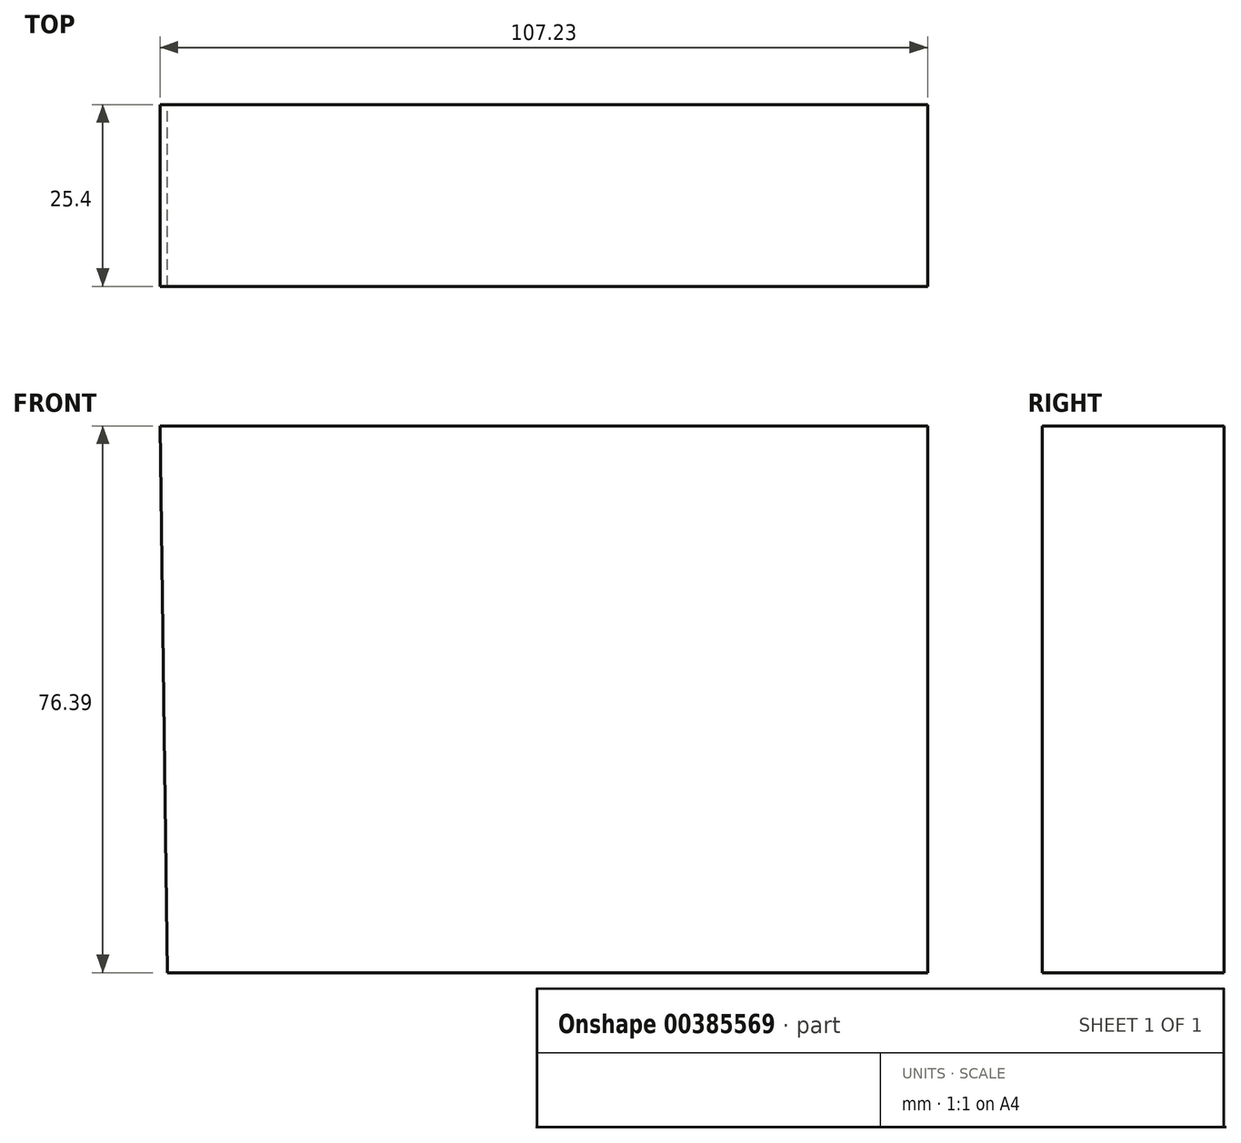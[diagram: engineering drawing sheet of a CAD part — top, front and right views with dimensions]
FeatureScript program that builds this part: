
annotation { "Feature Type Name" : "Feature", "Feature Type Description" : "" }
export const myFeature = defineFeature(function(context is Context, id is Id, definition is map)
    precondition{}
    {
        {
            var Q0;
            Q0=qCreatedBy(makeId("Front.planeOp"),FACE);
            var sketch = newSketch(context, id + "F0", { "sketchPlane" : qUnion([Q0])});
            skLineSegment(sketch, "E0", {"start": v(-51.16, 63.01) * mm, "end": v(56.07, 63.01) * mm});
            skLineSegment(sketch, "E1", {"start": v(56.07, 63.01) * mm, "end": v(56.07, -13.38) * mm});
            skLineSegment(sketch, "E2", {"start": v(56.07, -13.38) * mm, "end": v(-50.14, -13.38) * mm});
            skLineSegment(sketch, "E3", {"start": v(-50.14, -13.38) * mm, "end": v(-51.16, 63.01) * mm});
            skSolve(sketch);
        }
        {
            var Q0;
            Q0=makeQuery(id+"F0.imprint","IMPRINT",FACE,{"disambiguationData":[TD([[makeQuery(id+"F0.imprint","IMPRINT",EDGE,{"derivedFrom":sQuery(id+"F0.wireOp",EDGE,"E0")}),-1.0]])]});
            extrude(context, id + "F1", {"entities" : qUnion([Q0]), "depth" : 25.4 * mm});
        }
    });
